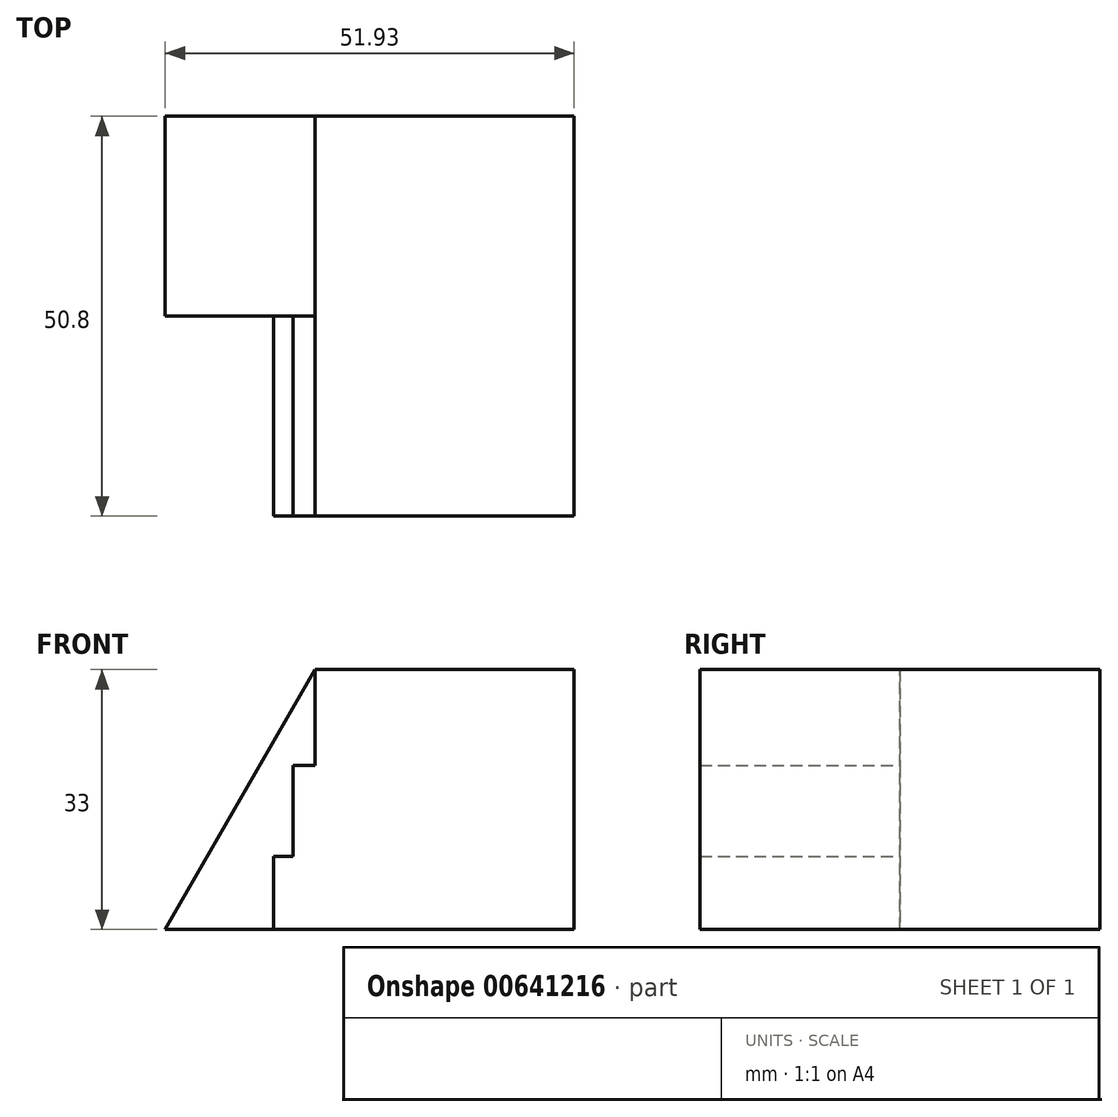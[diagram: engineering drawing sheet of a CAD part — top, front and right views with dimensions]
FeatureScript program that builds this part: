
annotation { "Feature Type Name" : "Feature", "Feature Type Description" : "" }
export const myFeature = defineFeature(function(context is Context, id is Id, definition is map)
    precondition{}
    {
        {
            var Q0;
            Q0=qCreatedBy(makeId("Front.planeOp"),FACE);
            var sketch = newSketch(context, id + "F0", { "sketchPlane" : qUnion([Q0])});
            skLineSegment(sketch, "E0", {"start": v(0, 0) * mm, "end": v(19.05, 33) * mm});
            skLineSegment(sketch, "E1", {"start": v(19.05, 33) * mm, "end": v(51.93, 33) * mm});
            skLineSegment(sketch, "E2", {"start": v(51.93, 33) * mm, "end": v(51.93, 0) * mm});
            skLineSegment(sketch, "E3", {"start": v(51.93, 0) * mm, "end": v(0, 0) * mm});
            skLineSegment(sketch, "E4", {"start": v(19.05, 33) * mm, "end": v(19.05, 20.81) * mm});
            skLineSegment(sketch, "E5", {"start": v(19.05, 20.81) * mm, "end": v(16.26, 20.81) * mm});
            skLineSegment(sketch, "E6", {"start": v(16.26, 20.81) * mm, "end": v(16.26, 9.3) * mm});
            skLineSegment(sketch, "E7", {"start": v(16.26, 9.3) * mm, "end": v(13.77, 9.3) * mm});
            skLineSegment(sketch, "E8", {"start": v(13.77, 9.3) * mm, "end": v(13.77, 0) * mm});
            skSolve(sketch);
        }
        {
            var Q0;
            Q0=makeQuery(id+"F0.imprint","IMPRINT",FACE,{"disambiguationData":[TD([[makeQuery(id+"F0.imprint","IMPRINT",EDGE,{"derivedFrom":sQuery(id+"F0.wireOp",EDGE,"E1")}),-1.0]])]});
            extrude(context, id + "F1", {"entities" : qUnion([Q0]), "depth" : 25.4 * mm, "offsetDistance" : 25.4 * mm});
        }
        {
            var Q0;
            Q0 = qSketchRegion(id + "F0", true);
            var Q1;
            Q1=makeQuery(id+"F1.opExtrude","CAP_FACE",FACE,{"disambiguationData":[OSD([sQuery(id+"F0.wireOp",EDGE,"E1"),sQuery(id+"F0.wireOp",EDGE,"E2"),sQuery(id+"F0.wireOp",EDGE,"E3"),sQuery(id+"F0.wireOp",EDGE,"E4"),sQuery(id+"F0.wireOp",EDGE,"E5"),sQuery(id+"F0.wireOp",EDGE,"E6"),sQuery(id+"F0.wireOp",EDGE,"E7"),sQuery(id+"F0.wireOp",EDGE,"CAcGXR8q-C2xx-52PN-w0Zr-ACBIedYtY4ab")])],"isStart":true});
            extrude(context, id + "F2", {"entities" : qUnion([Q0, Q1]), "operationType" : NewBodyOperationType.ADD, "oppositeDirection" : true, "depth" : 25.4 * mm, "offsetDistance" : 25.4 * mm});
        }
    });
